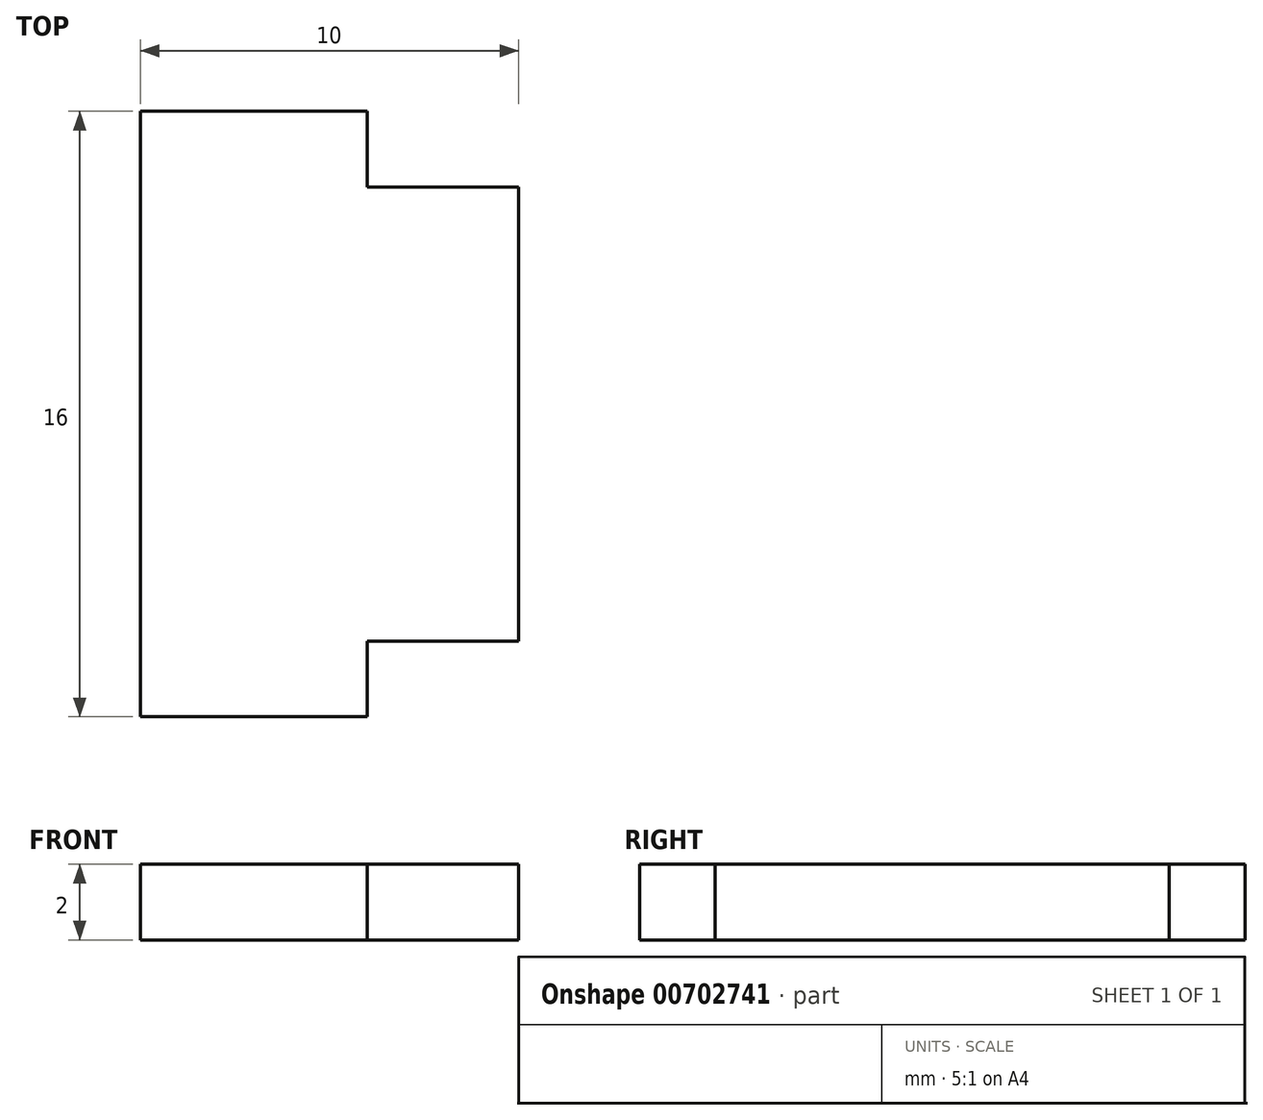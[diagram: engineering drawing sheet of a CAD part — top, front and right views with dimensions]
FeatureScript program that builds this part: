
annotation { "Feature Type Name" : "Feature", "Feature Type Description" : "" }
export const myFeature = defineFeature(function(context is Context, id is Id, definition is map)
    precondition{}
    {
        {
            var Q0;
            Q0=qCreatedBy(makeId("Top.planeOp"),FACE);
            var sketch = newSketch(context, id + "F0", { "sketchPlane" : qUnion([Q0])});
            skLineSegment(sketch, "E0.bottom", {"start": v(1, 8) * mm, "end": v(-5, 8) * mm});
            skLineSegment(sketch, "E0.top", {"start": v(1, -8) * mm, "end": v(-5, -8) * mm});
            skLineSegment(sketch, "E0.left", {"start": v(5, 6) * mm, "end": v(5, -6) * mm});
            skLineSegment(sketch, "E0.right", {"start": v(-5, 8) * mm, "end": v(-5, -8) * mm});
            skPoint(sketch, "E0.middle", {"position": v(0, 0) * mm});
            skLineSegment(sketch, "E1", {"start": v(1, -8) * mm, "end": v(1, -6) * mm});
            skLineSegment(sketch, "E2", {"start": v(5, -6) * mm, "end": v(1, -6) * mm});
            skLineSegment(sketch, "E3", {"start": v(-5, 0) * mm, "end": v(5, 0) * mm, "construction": true});
            skLineSegment(sketch, "E4.MirrorCS", {"start": v(5, 6) * mm, "end": v(1, 6) * mm});
            skPoint(sketch, "E5.orphan", {"position": v(-5, -6) * mm});
            skLineSegment(sketch, "E6.trimOffspring", {"start": v(1, 6) * mm, "end": v(1, 8) * mm});
            skPoint(sketch, "E7.orphan", {"position": v(-5, 6) * mm});
            skPoint(sketch, "E8.orphan", {"position": v(5, 8) * mm});
            skPoint(sketch, "E9.orphan", {"position": v(5, -8) * mm});
            skSolve(sketch);
        }
        {
            var Q0;
            Q0 = qSketchRegion(id + "F0", true);
            extrude(context, id + "F1", {"entities" : qUnion([Q0]), "depth" : 2 * mm, "offsetDistance" : 25 * mm});
        }
    });
